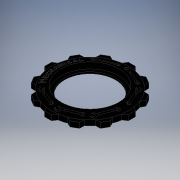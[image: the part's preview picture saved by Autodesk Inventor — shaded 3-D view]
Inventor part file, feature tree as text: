
AUTODESK INVENTOR PART (.ipt)
format: ipt  version: 2016 (Build 200138000, 138)  size: 927,744 bytes
history: native  units: in
note: dims shown in document units (in); Inventor stores cm internally (conversion verified against a paired STEP export)
features: sketch x4, projected_geometry x4, extrude x3, pattern_circular x2, revolve x1, plane x1, fillet x1, mirror x1
ambient origin geometry x8: Origin, YZ Plane, XZ Plane, XY Plane, X Axis, Y Axis, Z Axis, Center Point
bodies: Solid1 (feature_tree)
feature tree (17):
  revolve  "Revolution1"  [1 undecoded]
  plane  "Work Plane1"
  extrude  "Extrusion1"  Depth=0.05in
  pattern_circular  "Circular Pattern1"  Angle=90.0deg  [1 undecoded]
  extrude  "Extrusion2"  Depth=0.125in
  extrude  "Extrusion3"  Depth=0.125in
  fillet  "Fillet1"  Radius=0.2in
  pattern_circular  "Circular Pattern2"  [2 undecoded]
  mirror  "Mirror1"
  sketch  "Sketch1"  dims[d0=0.8265in d1=0.175in]
  sketch  "Sketch2"  dims[d2=0.05in d3=0.1in]
  sketch  "Sketch3"  dims[d4=0.15in]
  projected_geometry  "Projected Loop1"
  projected_geometry  "Projected Loop2"
  sketch  "Sketch4"  dims[d5=0.275in d6=90.0deg d7=0.1in d8=0.35in d9=0.2in d10=0.1in d11=1.0in d12=0.0in d13=4.7244in d14=360.0deg d16=0.075in d17=1.0in d18=0.0in d19=0.1in d20=0.025in d22=0.15in d23=0.25in d24=0.14in d25=135.0deg d26=0.05in d27=0.025in d28=0.5in d29=0.2in d30=0.065in d31=1.0in d32=0.0in d33=0.125in d34=1.1811in d35=90.0deg]
  projected_geometry  "Projected Loop3"
  projected_geometry  "Projected Loop4"
note: 4 required parameter values undecoded (feature->parameter linkage not recoverable at this tier; creation-order binding heuristic only, values carry confidence <= 0.55)